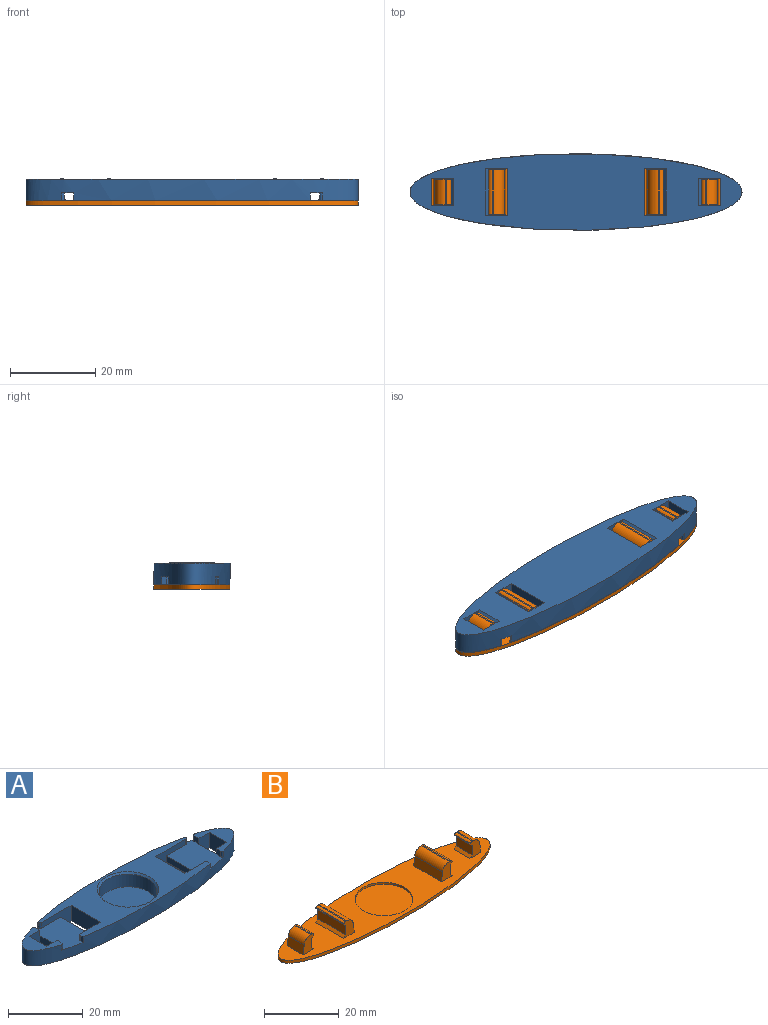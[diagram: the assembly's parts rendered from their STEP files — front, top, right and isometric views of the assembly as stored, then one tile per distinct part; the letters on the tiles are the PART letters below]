
ASSEMBLY  parts=2 mates=1
PART A: 46 faces, bbox 78x18x5 mm
  f0: plane 6.5x2mm, normal (1,0,0), area 13mm2, adj f17,f19,f25,f42
  f1: plane 6.5x2mm, normal (-1,0,0), area 13mm2, adj f20,f21,f30,f45
  f2: plane 55.6x18mm, normal (0,0,1), area 427.7mm2, adj f5,f9,f10,f12,f14,f15,f16,f26
  f3: plane 11.18x9mm, normal (0,0,1), area 44.6mm2, adj f5,f17,f18,f19,f23,f24,f36,f37
  f4: plane 11.18x9mm, normal (0,0,1), area 44.6mm2, adj f5,f20,f21,f22,f28,f29,f34,f35
  f5: extruded ~78x18mm, area 795.5mm2, adj f2,f3,f4,f6,f25,f26,f27,f30
  f6: plane 78x18mm, normal (0,0,-1), area 920.7mm2, adj f5,f9,f10,f12,f14,f15,f16,f17
  f7: cylinder r=7.7mm len=15.4mm, axis (0,0,1), area 198.4mm2, adj f8,f33
  f8: plane 15.4x15.4mm, normal (0,0,1), area 186.3mm2, adj f7
  f9: plane 11x5mm, normal (-1,0,0), area 55mm2, adj f2,f6,f10,f12
  f10: plane 11.3x5mm, normal (0,-1,0), area 33.9mm2, adj f2,f6,f9,f11,f30,f41,f44
  f11: plane 11x2mm, normal (1,0,0), area 22mm2, adj f10,f12,f30,f44
  f12: plane 7.5x5mm, normal (0,1,0), area 27mm2, adj f2,f6,f9,f11,f30,f40,f44
  f13: plane 11x2mm, normal (-1,0,0), area 22mm2, adj f14,f16,f25,f43
  f14: plane 11.3x5mm, normal (0,-1,0), area 33.9mm2, adj f2,f6,f13,f15,f25,f38,f43
  f15: plane 11x5mm, normal (1,0,0), area 55mm2, adj f2,f6,f14,f16
  f16: plane 7.5x5mm, normal (0,1,0), area 27mm2, adj f2,f6,f13,f15,f25,f39,f43
  f17: plane 5.2x5mm, normal (0,1,0), area 20.7mm2, adj f0,f3,f6,f18,f24,f42
  f18: plane 6.5x5mm, normal (-1,0,0), area 32.5mm2, adj f3,f6,f17,f19
  f19: plane 5.2x5mm, normal (0,-1,0), area 20.7mm2, adj f0,f3,f6,f18,f23,f42
  f20: plane 5.2x5mm, normal (0,1,0), area 20.7mm2, adj f1,f4,f6,f22,f29,f45
  f21: plane 5.2x5mm, normal (0,-1,0), area 20.7mm2, adj f1,f4,f6,f22,f28,f45
  f22: plane 6.5x5mm, normal (1,0,0), area 32.5mm2, adj f4,f6,f20,f21
  f23: plane 1.84x1.8mm, normal (-1,0,0), area 3.3mm2, adj f3,f19,f25,f36
  f24: plane 1.84x1.8mm, normal (-1,0,0), area 3.3mm2, adj f3,f17,f25,f37
  f25: plane 13.41x10.64mm, normal (0,0,1), area 117.3mm2, adj f0,f5,f13,f14,f16,f23,f24,f26
  f26: plane 1.8x0.31mm, normal (1,0,0), area 0.6mm2, adj f2,f5,f25,f38
  f27: plane 1.8x1.09mm, normal (1,0,0), area 2mm2, adj f2,f5,f25,f39
  f28: plane 1.84x1.8mm, normal (1,0,0), area 3.3mm2, adj f4,f21,f30,f34
  f29: plane 1.84x1.8mm, normal (1,0,0), area 3.3mm2, adj f4,f20,f30,f35
  f30: plane 13.41x10.64mm, normal (0,0,1), area 117.3mm2, adj f1,f5,f10,f11,f12,f28,f29,f31
  f31: plane 1.8x1.09mm, normal (-1,0,0), area 2mm2, adj f2,f5,f30,f40
  f32: plane 1.8x0.31mm, normal (-1,0,0), area 0.6mm2, adj f2,f5,f30,f41
  f33: cone r=7.7mm half-angle=45deg, axis (0,0,1), area 35.3mm2, adj f2,f7
  f34: cylinder r=0.5mm len=1.8mm, axis (0,0,-1), area 1.7mm2, adj f4,f5,f28,f30
  f35: cylinder r=0.5mm len=1.8mm, axis (0,0,-1), area 1.7mm2, adj f4,f5,f29,f30
  f36: cylinder r=0.5mm len=1.8mm, axis (0,0,-1), area 1.7mm2, adj f3,f5,f23,f25
  f37: cylinder r=0.5mm len=1.8mm, axis (0,0,-1), area 1.7mm2, adj f3,f5,f24,f25
  f38: cylinder r=0.5mm len=1.8mm, axis (0,0,1), area 1.4mm2, adj f2,f14,f25,f26
  f39: cylinder r=0.5mm len=1.8mm, axis (0,0,1), area 1.4mm2, adj f2,f16,f25,f27
  f40: cylinder r=0.5mm len=1.8mm, axis (0,0,1), area 1.4mm2, adj f2,f12,f30,f31
  f41: cylinder r=0.5mm len=1.8mm, axis (0,0,1), area 1.4mm2, adj f2,f10,f30,f32
  f42: plane 6.5x1.2mm, normal (0.71,0,-0.71), area 11mm2, adj f0,f6,f17,f19
  f43: plane 11x1.2mm, normal (-0.71,0,-0.71), area 18.7mm2, adj f6,f13,f14,f16
  f44: plane 11x1.2mm, normal (0.71,0,-0.71), area 18.7mm2, adj f6,f10,f11,f12
  f45: plane 6.5x1.2mm, normal (-0.71,0,-0.71), area 11mm2, adj f1,f6,f20,f21
PART B: 47 faces, bbox 78x18x6.2 mm
  f0: plane 5.2x4.1mm, normal (0,1,0), area 15.4mm2, adj f2,f8,f10,f21,f28,f31,f34,f37
  f1: plane 5.2x4.1mm, normal (0,-1,0), area 15.4mm2, adj f2,f8,f10,f21,f28,f31,f34,f37
  f2: plane 10.5x0.33mm, normal (0,0,1), area 3.5mm2, adj f0,f1,f40,f43
  f3: plane 5.2x4.1mm, normal (0,1,0), area 15.4mm2, adj f5,f7,f10,f20,f25,f32,f33,f35
  f4: plane 5.2x4.1mm, normal (0,-1,0), area 15.4mm2, adj f5,f7,f10,f20,f25,f32,f33,f35
  f5: plane 6x0.33mm, normal (0,0,1), area 2mm2, adj f3,f4,f42,f44
  f6: plane 5.2x4.1mm, normal (0,-1,0), area 15.4mm2, adj f10,f18,f19,f23,f26,f30,f36,f41
  f7: plane 6x0.8mm, normal (-0.71,0,-0.71), area 6.8mm2, adj f3,f4,f20,f32
  f8: plane 10.5x0.8mm, normal (-0.71,0,-0.71), area 11.9mm2, adj f0,f1,f21,f31
  f9: plane 5.2x4.1mm, normal (0,1,0), area 15.4mm2, adj f10,f18,f19,f23,f26,f30,f36,f41
  f10: plane 78x18mm, normal (0,0,1), area 781.1mm2, adj f0,f1,f3,f4,f6,f9,f11,f13
  f11: extruded ~78x18mm, area 166.1mm2, adj f10,f12
  f12: plane 78x18mm, normal (0,0,-1), area 1102.7mm2, adj f11
  f13: cylinder r=7.7mm len=15.4mm, axis (0,0,1), area 29mm2, adj f10,f14
  f14: plane 15.4x15.4mm, normal (0,0,1), area 186.3mm2, adj f13
  f15: plane 5.2x4.1mm, normal (0,1,0), area 15.4mm2, adj f10,f17,f22,f24,f27,f29,f38,f39
  f16: plane 5.2x4.1mm, normal (0,-1,0), area 15.4mm2, adj f10,f17,f22,f24,f27,f29,f38,f39
  f17: plane 6x0.35mm, normal (0,0,1), area 2.1mm2, adj f15,f16,f39,f45
  f18: plane 10.5x0.35mm, normal (0,0,1), area 3.7mm2, adj f6,f9,f41,f46
  f19: plane 10.5x3mm, normal (1,0,0), area 31.5mm2, adj f6,f9,f23,f26
  f20: plane 6x3mm, normal (-1,0,0), area 18mm2, adj f3,f4,f7,f25
  f21: plane 10.5x3mm, normal (-1,0,0), area 31.5mm2, adj f0,f1,f8,f28
  f22: plane 6x3mm, normal (1,0,0), area 18mm2, adj f15,f16,f24,f27
  f23: plane 10.5x0.8mm, normal (0.71,0,-0.71), area 11.9mm2, adj f6,f9,f19,f30
  f24: plane 6x0.8mm, normal (0.71,0,-0.71), area 6.8mm2, adj f15,f16,f22,f29
  f25: plane 6x0.8mm, normal (-0.71,0,0.71), area 6.8mm2, adj f3,f4,f10,f20
  f26: plane 10.5x0.8mm, normal (0.71,0,0.71), area 11.9mm2, adj f6,f9,f10,f19
  f27: plane 6x0.8mm, normal (0.71,0,0.71), area 6.8mm2, adj f10,f15,f16,f22
  f28: plane 10.5x0.8mm, normal (-0.71,0,0.71), area 11.9mm2, adj f0,f1,f10,f21
  f29: plane 6x0.1mm, normal (1,0,0), area 0.6mm2, adj f15,f16,f24,f45
  f30: plane 10.5x0.1mm, normal (1,0,0), area 1.1mm2, adj f6,f9,f23,f46
  f31: plane 10.5x0.1mm, normal (-1,0,0), area 1.1mm2, adj f0,f1,f8,f34
  f32: plane 6x0.1mm, normal (-1,0,0), area 0.6mm2, adj f3,f4,f7,f33
  f33: plane 6x0.14mm, normal (-0.77,0,0.64), area 1.1mm2, adj f3,f4,f32,f44
  f34: plane 10.5x0.14mm, normal (-0.77,0,0.64), area 2mm2, adj f0,f1,f31,f43
  f35: plane 6x3.03mm, normal (0.99,0,0.13), area 18.3mm2, adj f3,f4,f10,f42
  f36: plane 10.5x3.03mm, normal (-0.99,0,0.13), area 32.1mm2, adj f6,f9,f10,f41
  f37: plane 10.5x3.03mm, normal (0.99,0,0.13), area 32.1mm2, adj f0,f1,f10,f40
  f38: plane 6x3.03mm, normal (-0.99,0,0.13), area 18.3mm2, adj f10,f15,f16,f39
  f39: cylinder r=2.5mm len=6mm, axis (0,1,0), area 21.6mm2, adj f15,f16,f17,f38
  f40: cylinder r=2.5mm len=10.5mm, axis (0,1,0), area 37.8mm2, adj f0,f1,f2,f37
  f41: cylinder r=2.5mm len=10.5mm, axis (0,1,0), area 37.8mm2, adj f6,f9,f18,f36
  f42: cylinder r=2.5mm len=6mm, axis (0,1,0), area 21.6mm2, adj f3,f4,f5,f35
  f43: cylinder r=1mm len=10.5mm, axis (0,1,0), area 9.2mm2, adj f0,f1,f2,f34
  f44: cylinder r=1mm len=6mm, axis (0,1,0), area 5.2mm2, adj f3,f4,f5,f33
  f45: cylinder r=1mm len=6mm, axis (0,1,0), area 6.3mm2, adj f15,f16,f17,f29
  f46: cylinder r=1mm len=10.5mm, axis (0,1,0), area 11mm2, adj f6,f9,f18,f30
PLACE A rot(axis=(1,0,0),180deg) t=(-2.24,1.87,9.81)mm fixed
PLACE B t=(-2.24,1.87,3.72)mm
MATE slider A.f7 <-> B.f13  axis (0,0,-1) through (-2.24,1.87,7.36)mm
